# Revit family: G561_Casement_Inswing_Window-Peerless
name_source: partatom
category: Windows
units: mm (PartAtom-declared; Revit-internal decimal feet)

## family parameters
Always vertical = Yes
Cut with Voids When Loaded = No
Host = Wall
OmniClass Number = 23.30.20.00
OmniClass Title = Windows
Room Calculation Point = No
Shared = No

## types (1)
- G561 Casement Inswing 36" x 48"
    04 CSI = 08 50 00
    Analytic Construction = <None>
    Default Sill Height = 36 "
    Description = G561 is an ultra-performing casement inswing window used in buildings with the most stringent thermal requirements and window wall applications.
    Height = 48 "
    Manufacturer = Peerless Products, Inc.
    Manufacturer Fax = 620-224-3107
    Model = G561
    Product Data Sheet URL = https://www.peerlessproducts.com
    Product Page URL = https://peerlessproducts.concora.com
    Rough Height = 48.25 "
    Rough Width = 36.25 "
    URL = https://www.peerlessproducts.com
    Wall Closure = By host
    Warranty URL = https://smartbim-library-production.s3.amazonaws.com
    Weight (lbs) = 49
    Width = 36 "

## geometry (parser evidence)
native form markers: Sweep x2
no freeform markers — native parametric forms only
